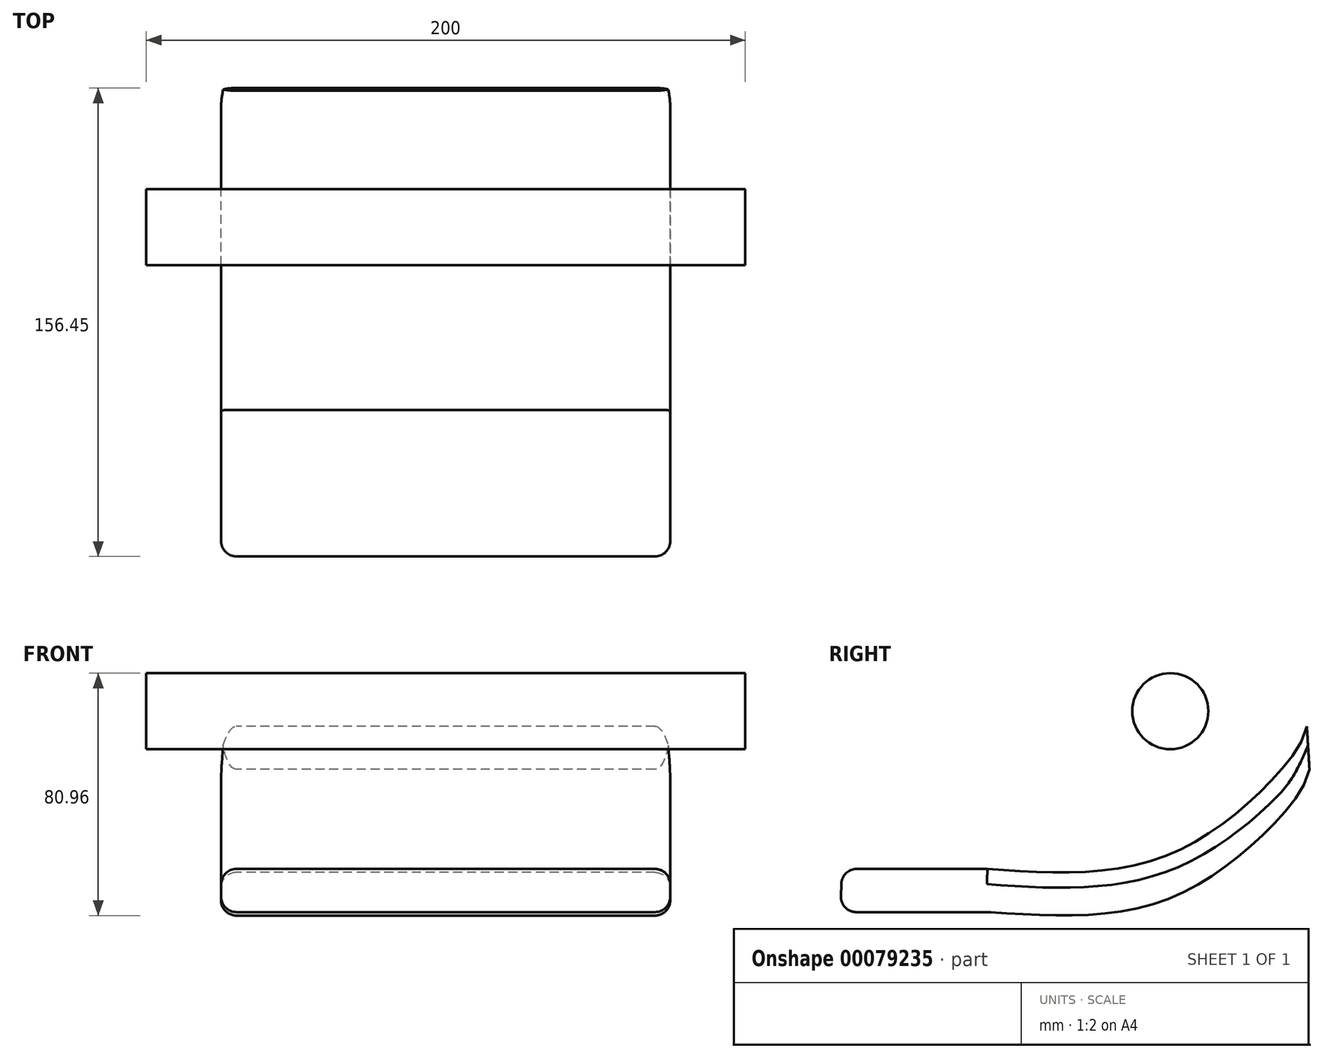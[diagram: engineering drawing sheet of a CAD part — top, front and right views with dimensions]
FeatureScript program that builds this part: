
annotation { "Feature Type Name" : "Feature", "Feature Type Description" : "" }
export const myFeature = defineFeature(function(context is Context, id is Id, definition is map)
    precondition{}
    {
        {
            var Q0;
            Q0=qCreatedBy(makeId("Right.planeOp"),FACE);
            var sketch = newSketch(context, id + "F0", { "sketchPlane" : qUnion([Q0])});
            skLineSegment(sketch, "E0", {"start": v(-76.77, 0.1) * mm, "end": v(-26.77, 0.1) * mm});
            skFitSpline(sketch, "E1", {"points": [v(-26.77, 0.1) * mm, v(36.35, 6.06) * mm, v(76.28, 39.71) * mm, v(79.87, 47.8) * mm], "startDerivative": vector(148.5, -10.33) * mm, "endDerivative": vector(11.1, 41.05) * mm});
            skFitSpline(sketch, "E2", {"points": [v(-27.66, 14.5) * mm, v(35.46, 20.44) * mm, v(75.4, 54.1) * mm, v(78.99, 62.17) * mm], "startDerivative": vector(148.5, -10.33) * mm, "endDerivative": vector(11.1, 41.05) * mm});
            skLineSegment(sketch, "E3", {"start": v(79.87, 47.8) * mm, "end": v(78.99, 62.17) * mm});
            skLineSegment(sketch, "E4", {"start": v(-27.66, 14.5) * mm, "end": v(-76.24, 14.5) * mm});
            skLineSegment(sketch, "E5", {"start": v(-76.77, 0.1) * mm, "end": v(-76.24, 14.5) * mm});
            skSolve(sketch);
        }
        {
            var Q0;
            Q0 = qSketchRegion(id + "F0", true);
            var Q1;
            Q1=sQuery(id+"F0.wireOp",EDGE,"E1");
            var Q2;
            Q2=sQuery(id+"F0.wireOp",EDGE,"E0");
            extrude(context, id + "F1", {"entities" : qUnion([Q0]), "surfaceEntities" : qUnion([Q1, Q2]), "endBound" : BoundingType.SYMMETRIC, "depth" : 150 * mm});
        }
        {
            var Q0;
            Q0=qCreatedBy(makeId("Right.planeOp"),FACE);
            var sketch = newSketch(context, id + "F2", { "sketchPlane" : qUnion([Q0])});
            skCircle(sketch, "E6", {"center": v(33.4, 67.22) * mm, "radius": 12.7 * mm});
            skSolve(sketch);
        }
        {
            var Q0;
            Q0=makeQuery(id+"F2.imprint","IMPRINT",FACE,{"disambiguationData":[TD([[makeQuery(id+"F2.imprint","IMPRINT",EDGE,{"derivedFrom":sQuery(id+"F2.wireOp",EDGE,"E6")}),1.0]])]});
            extrude(context, id + "F3", {"entities" : qUnion([Q0]), "endBound" : BoundingType.SYMMETRIC, "depth" : 200 * mm});
        }
        {
            var Q0;
            Q0=makeQuery(id+"F1.opExtrude","CAP_FACE",FACE,{"disambiguationData":[OSD([sQuery(id+"F0.wireOp",EDGE,"E0"),sQuery(id+"F0.wireOp",EDGE,"E1"),sQuery(id+"F0.wireOp",EDGE,"E2"),sQuery(id+"F0.wireOp",EDGE,"E3"),sQuery(id+"F0.wireOp",EDGE,"E4"),sQuery(id+"F0.wireOp",EDGE,"E5")])],"isStart":true});
            var Q1;
            Q1=makeQuery(id+"F1.opExtrude","SWEPT_FACE",FACE,{"disambiguationData":[OSD([sQuery(id+"F0.wireOp",EDGE,"E0")])]});
            var Q2;
            Q2=makeQuery(id+"F1.opExtrude","CAP_FACE",FACE,{"disambiguationData":[OSD([sQuery(id+"F0.wireOp",EDGE,"E0"),sQuery(id+"F0.wireOp",EDGE,"E1"),sQuery(id+"F0.wireOp",EDGE,"E2"),sQuery(id+"F0.wireOp",EDGE,"E3"),sQuery(id+"F0.wireOp",EDGE,"E4"),sQuery(id+"F0.wireOp",EDGE,"E5")])],"isStart":false});
            var Q3;
            Q3=makeQuery(id+"F1.opExtrude","SWEPT_FACE",FACE,{"disambiguationData":[OSD([sQuery(id+"F0.wireOp",EDGE,"E5")])]});
            fillet(context, id + "F4", {"entities" : qUnion([Q0, Q1, Q2, Q3]), "radius" : 5.08 * mm, "tangentPropagation" : true, "allowEdgeOverflow" : false});
        }
    });
